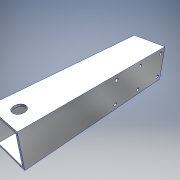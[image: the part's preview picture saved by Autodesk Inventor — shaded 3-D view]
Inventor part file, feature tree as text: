
AUTODESK INVENTOR PART (.ipt)
format: ipt  version: 2019 (Build 230136000, 136)  size: 144,384 bytes
history: native  units: in
note: dims shown in document units (in); Inventor stores cm internally (conversion verified against a paired STEP export)
features: extrude x3, sketch x3
ambient origin geometry x8: Origin, YZ Plane, XZ Plane, XY Plane, X Axis, Y Axis, Z Axis, Center Point
bodies: Solid1 (feature_tree)
feature tree (6):
  extrude  "Extrusion1"  Depth=0.125in
  extrude  "Extrusion2"  Depth=9.0in
  extrude  "Extrusion6"  Depth=3.5in
  sketch  "Sketch1"  dims[d0=2.0in d1=0.125in]
  sketch  "Sketch2"  dims[d2=9.0in d3=0.0in d4=0.21in]
  sketch  "Sketch4"  dims[d5=0.3in d6=3.5in d7=0.7in d8=18.0in d9=0.0in d13=0.625in d14=0.75in d17=0.19in d18=1.0in d21=1.0in d22=0.0in]
